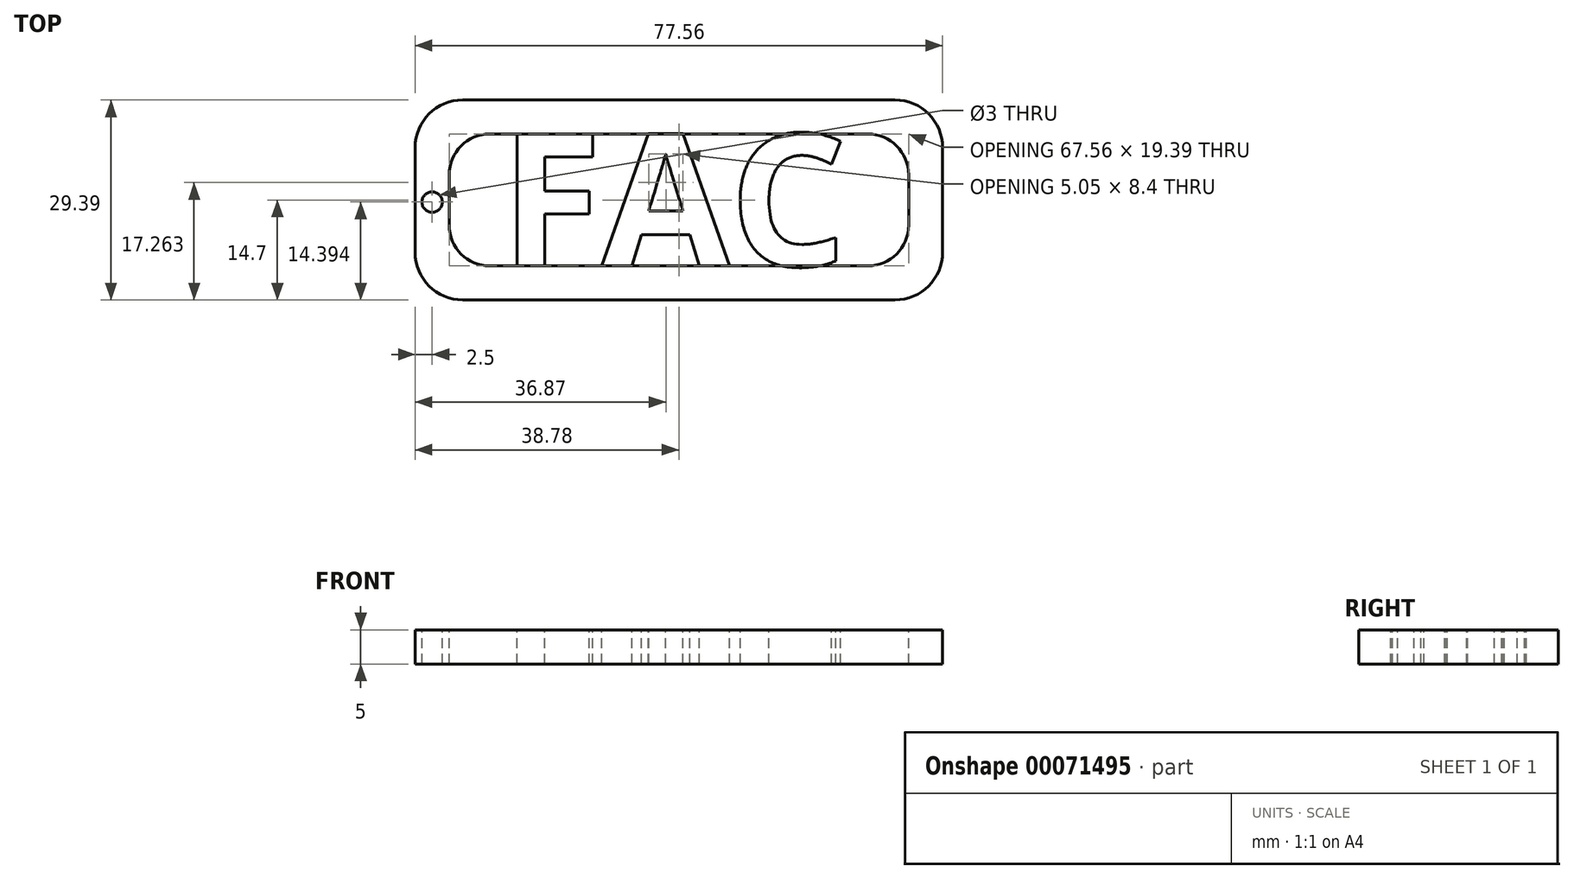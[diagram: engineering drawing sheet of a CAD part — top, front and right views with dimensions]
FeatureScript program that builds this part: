
annotation { "Feature Type Name" : "Feature", "Feature Type Description" : "" }
export const myFeature = defineFeature(function(context is Context, id is Id, definition is map)
    precondition{}
    {
        {
            var Q0;
            Q0=qCreatedBy(makeId("Top.planeOp"),FACE);
            var sketch = newSketch(context, id + "F0", { "sketchPlane" : qUnion([Q0])});
            skText(sketch, "E0", { "text": "FAC", "fontName": "OpenSans-Bold.ttf"});
            const initialGuessF0  = {"E0": [0, -0.01956, 1, 0, 0.01956]};
            skSetInitialGuess(sketch, initialGuessF0);
            skSolve(sketch);
        }
        {
            var Q0;
            Q0=qSketchRegion(id+"F0",true);
            extrude(context, id + "F1", {"entities" : qUnion([Q0]), "oppositeDirection" : true, "depth" : 5 * mm});
        }
        {
            var Q0;
            Q0=qCreatedBy(makeId("Top.planeOp"),FACE);
            var sketch = newSketch(context, id + "F2", { "sketchPlane" : qUnion([Q0])});
            skLineSegment(sketch, "E1.bottom", {"start": v(-7.56, -0.17) * mm, "end": v(60, -0.17) * mm});
            skLineSegment(sketch, "E1.top", {"start": v(-7.56, -19.56) * mm, "end": v(60, -19.56) * mm});
            skLineSegment(sketch, "E1.left", {"start": v(-7.56, -0.17) * mm, "end": v(-7.56, -19.56) * mm});
            skLineSegment(sketch, "E1.right", {"start": v(60, -0.17) * mm, "end": v(60, -19.56) * mm});
            skLineSegment(sketch, "E2.bottom", {"start": v(-12.56, 4.83) * mm, "end": v(65, 4.83) * mm});
            skLineSegment(sketch, "E2.top", {"start": v(-12.56, -24.56) * mm, "end": v(65, -24.56) * mm});
            skLineSegment(sketch, "E2.left", {"start": v(-12.56, 4.83) * mm, "end": v(-12.56, -24.56) * mm});
            skLineSegment(sketch, "E2.right", {"start": v(65, 4.83) * mm, "end": v(65, -24.56) * mm});
            skSolve(sketch);
        }
        {
            var Q0;
            Q0 = qSketchRegion(id + "F2", true);
            extrude(context, id + "F3", {"entities" : qUnion([Q0]), "oppositeDirection" : true, "depth" : 5 * mm});
        }
        {
            var Q0;
            Q0=makeQuery(id+"F3.opExtrude","SWEPT_EDGE",EDGE,{"disambiguationData":[OSD([sQuery(id+"F2.wireOp",EDGE,"E1.bottom"),sQuery(id+"F2.wireOp",EDGE,"E1.left")])]});
            var Q1;
            Q1=makeQuery(id+"F3.opExtrude","SWEPT_EDGE",EDGE,{"disambiguationData":[OSD([sQuery(id+"F2.wireOp",EDGE,"E1.top"),sQuery(id+"F2.wireOp",EDGE,"E1.left")])]});
            var Q2;
            Q2=makeQuery(id+"F3.opExtrude","SWEPT_EDGE",EDGE,{"disambiguationData":[OSD([sQuery(id+"F2.wireOp",EDGE,"E1.bottom"),sQuery(id+"F2.wireOp",EDGE,"E1.right")])]});
            var Q3;
            Q3=makeQuery(id+"F3.opExtrude","SWEPT_EDGE",EDGE,{"disambiguationData":[OSD([sQuery(id+"F2.wireOp",EDGE,"E1.top"),sQuery(id+"F2.wireOp",EDGE,"E1.right")])]});
            fillet(context, id + "F4", {"entities" : qUnion([Q0, Q1, Q2, Q3]), "radius" : 6 * mm, "tangentPropagation" : true, "allowEdgeOverflow" : false});
        }
        {
            var Q0;
            Q0=makeQuery(id+"F3.opExtrude","SWEPT_EDGE",EDGE,{"disambiguationData":[OSD([sQuery(id+"F2.wireOp",EDGE,"E2.bottom"),sQuery(id+"F2.wireOp",EDGE,"E2.left")])]});
            var Q1;
            Q1=makeQuery(id+"F3.opExtrude","SWEPT_EDGE",EDGE,{"disambiguationData":[OSD([sQuery(id+"F2.wireOp",EDGE,"E2.top"),sQuery(id+"F2.wireOp",EDGE,"E2.left")])]});
            var Q2;
            Q2=makeQuery(id+"F3.opExtrude","SWEPT_EDGE",EDGE,{"disambiguationData":[OSD([sQuery(id+"F2.wireOp",EDGE,"E2.bottom"),sQuery(id+"F2.wireOp",EDGE,"E2.right")])]});
            var Q3;
            Q3=makeQuery(id+"F3.opExtrude","SWEPT_EDGE",EDGE,{"disambiguationData":[OSD([sQuery(id+"F2.wireOp",EDGE,"E2.top"),sQuery(id+"F2.wireOp",EDGE,"E2.right")])]});
            fillet(context, id + "F5", {"entities" : qUnion([Q0, Q1, Q2, Q3]), "radius" : 7 * mm, "tangentPropagation" : true, "allowEdgeOverflow" : false});
        }
        {
            var Q0;
            Q0=makeQuery(id+"F3.opExtrude","CAP_FACE",FACE,{"disambiguationData":[OSD([sQuery(id+"F2.wireOp",EDGE,"E1.bottom"),sQuery(id+"F2.wireOp",EDGE,"E1.top"),sQuery(id+"F2.wireOp",EDGE,"E1.left"),sQuery(id+"F2.wireOp",EDGE,"E1.right"),sQuery(id+"F2.wireOp",EDGE,"E2.bottom"),sQuery(id+"F2.wireOp",EDGE,"E2.top"),sQuery(id+"F2.wireOp",EDGE,"E2.left"),sQuery(id+"F2.wireOp",EDGE,"E2.right")])],"isStart":true});
            var sketch = newSketch(context, id + "F6", { "sketchPlane" : qUnion([Q0])});
            skCircle(sketch, "E3", {"center": v(-10.06, -10.17) * mm, "radius": 1.5 * mm});
            skSolve(sketch);
        }
        {
            var Q0;
            Q0 = qSketchRegion(id + "F6", true);
            extrude(context, id + "F7", {"entities" : qUnion([Q0]), "operationType" : NewBodyOperationType.REMOVE, "endBound" : BoundingType.THROUGH_ALL, "oppositeDirection" : true, "depth" : 25 * mm});
        }
    });
